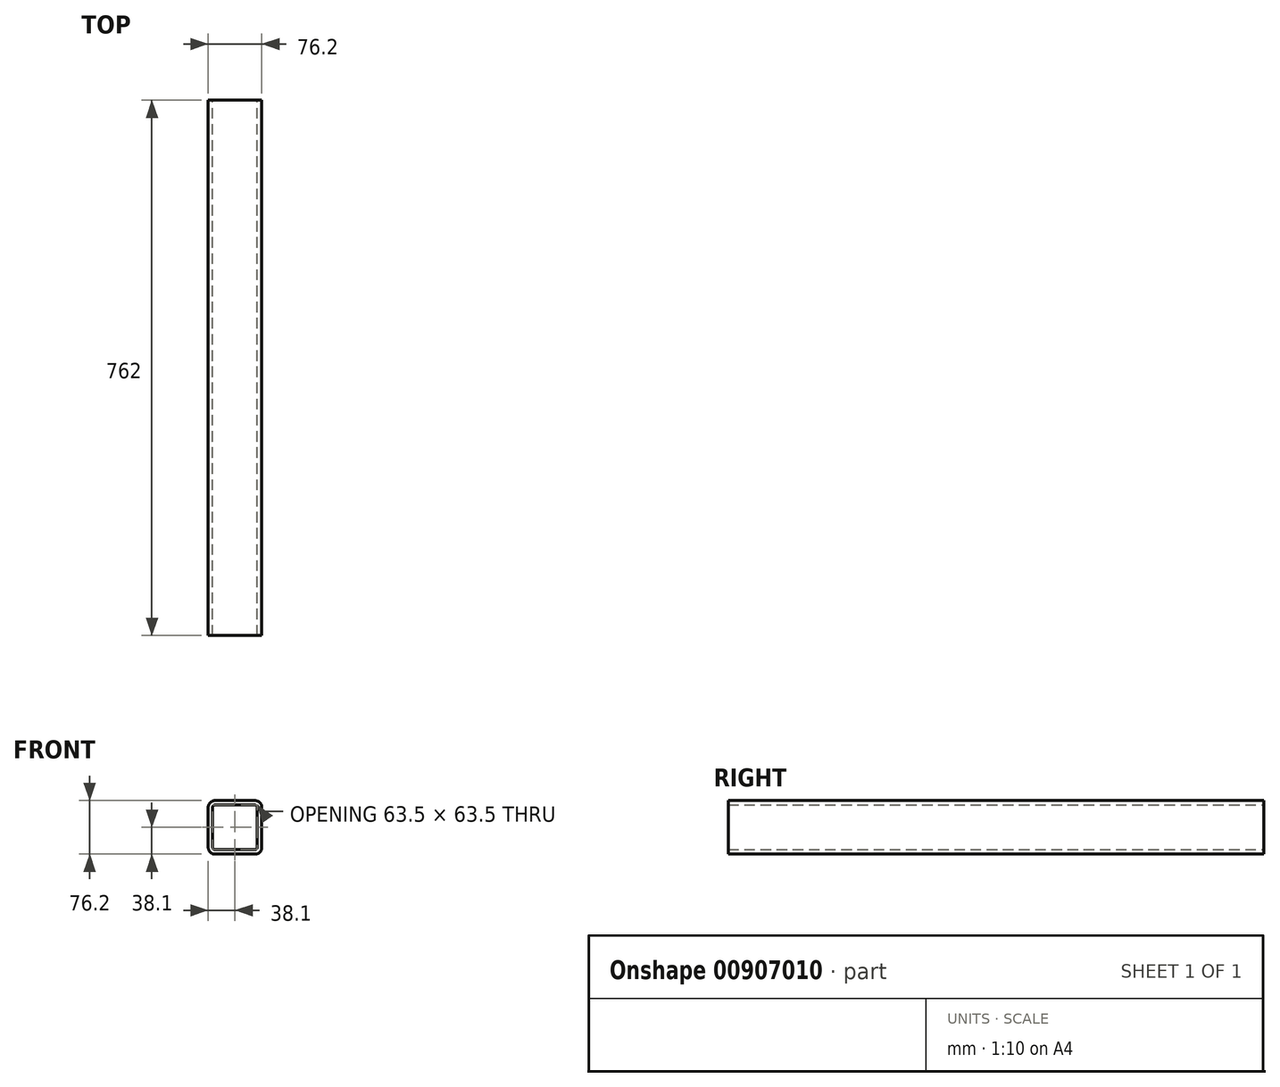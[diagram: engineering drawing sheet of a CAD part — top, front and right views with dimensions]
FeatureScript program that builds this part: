
annotation { "Feature Type Name" : "Feature", "Feature Type Description" : "" }
export const myFeature = defineFeature(function(context is Context, id is Id, definition is map)
    precondition{}
    {
        {
            var Q0;
            Q0=qCreatedBy(makeId("Front.planeOp"),FACE);
            var sketch = newSketch(context, id + "F0", { "sketchPlane" : qUnion([Q0])});
            skLineSegment(sketch, "E0.bottom", {"start": v(-28.58, -38.1) * mm, "end": v(28.58, -38.1) * mm});
            skLineSegment(sketch, "E0.top", {"start": v(-28.57, 38.1) * mm, "end": v(28.58, 38.1) * mm});
            skLineSegment(sketch, "E0.left", {"start": v(-38.1, -28.58) * mm, "end": v(-38.1, 28.58) * mm});
            skLineSegment(sketch, "E0.right", {"start": v(38.1, -28.58) * mm, "end": v(38.1, 28.58) * mm});
            skPoint(sketch, "E0.middle", {"position": v(0, 0) * mm});
            skPoint(sketch, "E1.visualSharp", {"position": v(-38.1, 38.1) * mm});
            skArc(sketch, "E1.filletArc", {"start": v(-28.57, 38.1) * mm, "mid": v(-35.31, 35.31) * mm, "end": v(-38.1, 28.58) * mm});
            skPoint(sketch, "E2.visualSharp", {"position": v(38.1, 38.1) * mm});
            skArc(sketch, "E2.filletArc", {"start": v(38.1, 28.58) * mm, "mid": v(35.31, 35.31) * mm, "end": v(28.58, 38.1) * mm});
            skPoint(sketch, "E3.visualSharp", {"position": v(-38.1, -38.1) * mm});
            skArc(sketch, "E3.filletArc", {"start": v(-38.1, -28.58) * mm, "mid": v(-35.31, -35.31) * mm, "end": v(-28.58, -38.1) * mm});
            skPoint(sketch, "E4.visualSharp", {"position": v(38.1, -38.1) * mm});
            skArc(sketch, "E4.filletArc", {"start": v(28.58, -38.1) * mm, "mid": v(35.31, -35.31) * mm, "end": v(38.1, -28.58) * mm});
            skArc(sketch, "E5.0", {"start": v(28.58, -31.75) * mm, "mid": v(30.82, -30.82) * mm, "end": v(31.75, -28.58) * mm});
            skLineSegment(sketch, "E5.1", {"start": v(-28.58, -31.75) * mm, "end": v(28.58, -31.75) * mm});
            skLineSegment(sketch, "E5.2", {"start": v(31.75, -28.58) * mm, "end": v(31.75, 28.58) * mm});
            skArc(sketch, "E5.3", {"start": v(-31.75, -28.58) * mm, "mid": v(-30.82, -30.82) * mm, "end": v(-28.58, -31.75) * mm});
            skArc(sketch, "E5.4", {"start": v(31.75, 28.58) * mm, "mid": v(30.82, 30.82) * mm, "end": v(28.58, 31.75) * mm});
            skLineSegment(sketch, "E5.5", {"start": v(-28.57, 31.75) * mm, "end": v(28.58, 31.75) * mm});
            skArc(sketch, "E5.6", {"start": v(-28.57, 31.75) * mm, "mid": v(-30.82, 30.82) * mm, "end": v(-31.75, 28.58) * mm});
            skLineSegment(sketch, "E5.7", {"start": v(-31.75, -28.58) * mm, "end": v(-31.75, 28.58) * mm});
            skSolve(sketch);
        }
        {
            var Q0;
            Q0=makeQuery(id+"F0.imprint","IMPRINT",FACE,{"disambiguationData":[TD([[makeQuery(id+"F0.imprint","IMPRINT",EDGE,{"derivedFrom":sQuery(id+"F0.wireOp",EDGE,"E0.bottom")}),1.0]])]});
            extrude(context, id + "F1", {"entities" : qUnion([Q0]), "depth" : 762 * mm, "offsetDistance" : 25.4 * mm});
        }
    });
